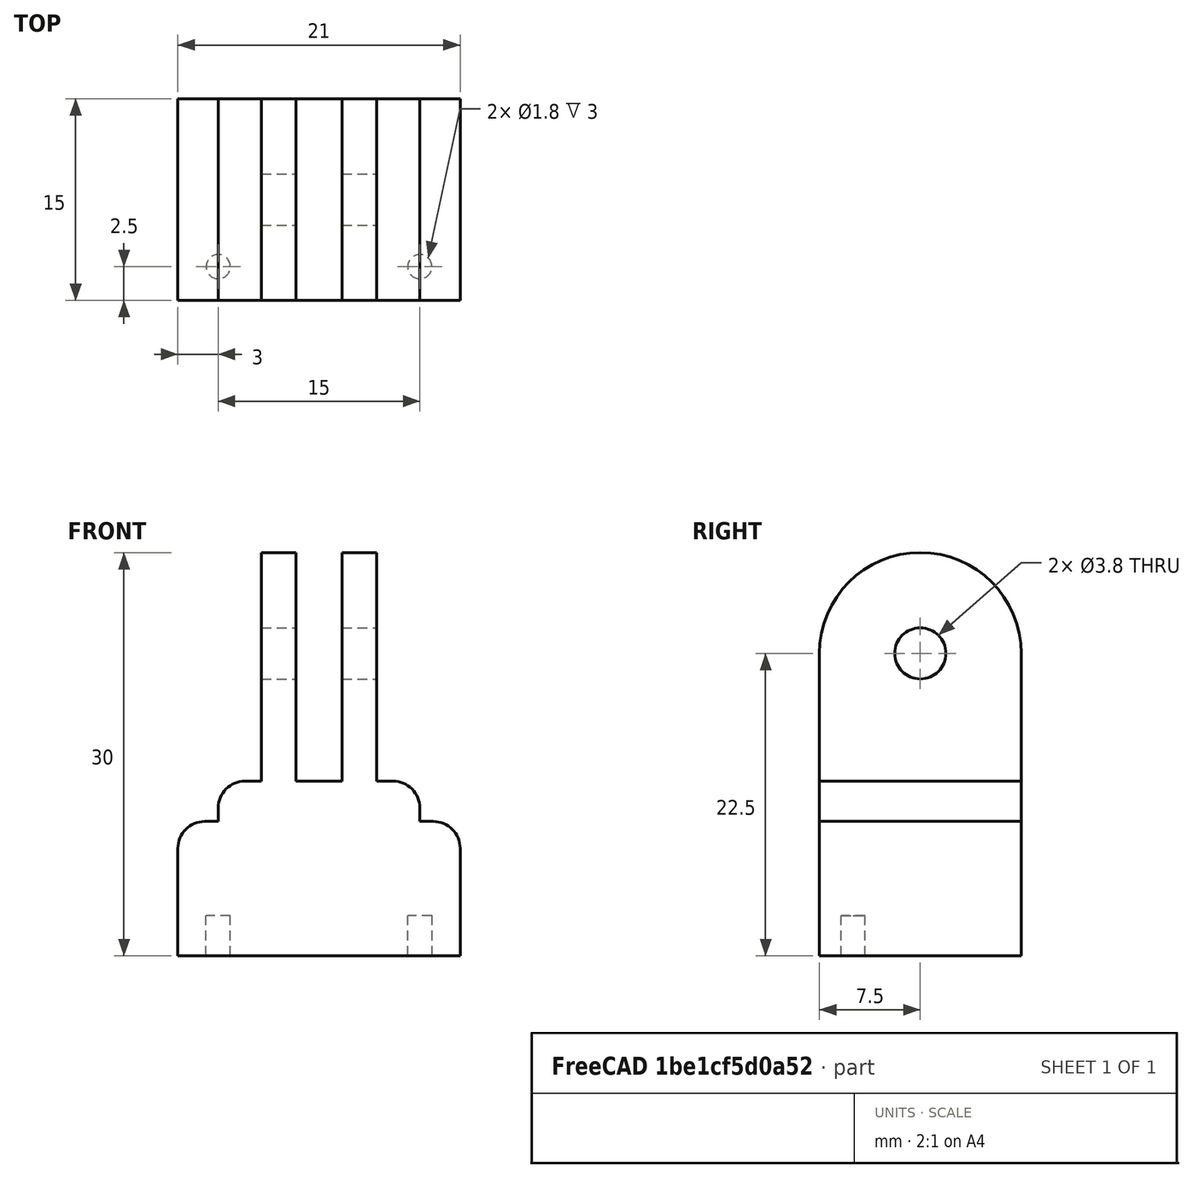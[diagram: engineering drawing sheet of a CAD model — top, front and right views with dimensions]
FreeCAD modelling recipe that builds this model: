
FCSTD DOCUMENT  (FreeCAD 0.19R23578 (Git))
Label: TCS3472RGBSensorSquare
License: FreeArt
LicenseURL: http://artlibre.org/licence/lal
objects: Part::Fillet×2, Spreadsheet::Sheet×1, Part::Cylinder×1, Part::FeaturePython×1, Part::Box×1, Part::Feature×1, Part::MultiFuse×1, Part::Cut×1, App::Part×1
note: 8 computed .brp shape members not serialized (recipe doc carries the construction recipe); baked Part::Feature solids carry a one-line shape summary decoded from their .brp

FEATURE [Spreadsheet::Sheet] Spreadsheet  label="p"
  cells = A1=pcb_x; B1(pcb_x)=21; A2=pcb_y; B2(pcb_y)=21; A3=pcb_z; B3(pcb_z)=1.7; A4=hole_dist_x; B4(hole_dist_x)=15; A5=hole_off_y; B5(hole_off_y)=2.5; A6=hole_r; B6(hole_r)=0.9; A7=sensor_hole_x; B7(sensor_hole_x)=2.6; A8=wall; B8(wall)=3; A9=stick_x; B9(stick_x)==pcb_x; A10=stick_y; B10(stick_y)=15; A11=stick_length; B11(stick_length)=10
FEATURE [Part::Cylinder] Cylinder  label="bolt hole"
  Angle = 360
  AttacherType = Attacher::AttachEngine3D
  Height = 3
  Radius = 0.9
  expr: Radius = <<p>>.hole_r
  expr: Height = <<p>>.wall
FEATURE [Part::FeaturePython] Array  label="bolt hole array"  # Draft array (typed FeaturePython)
  Angle = 360
  ArrayType = 0
  Axis = (0,0,1)
  Base = -> Cylinder
  Center = (0,0,0)
  Fuse = false
  IntervalAxis = (0,0,0)
  IntervalX = (15,0,0)
  IntervalY = (0,1,0)
  IntervalZ = (0,0,1)
  NumberPolar = 1
  NumberX = 2
  NumberY = 1
  NumberZ = 1
  Placement = pos=(3,2.5,0) rot=(0,0,1;0rad)
  expr: .Placement.Base.x = (<<p>>.pcb_x - <<p>>.hole_dist_x) / 2
  expr: .IntervalX.x = <<p>>.hole_dist_x
  expr: .Placement.Base.y = <<p>>.hole_off_y
FEATURE [Part::Box] Box002  label="stick cube"
  AttacherType = Attacher::AttachEngine3D
  Height = 10
  Length = 21
  Width = 15
  expr: Length = Spreadsheet.stick_x
  expr: Width = <<p>>.stick_y
  expr: Height = <<p>>.stick_length
FEATURE [Part::Feature] Cut001001  label="side 2 cut001"
  Placement = pos=(10.5,7.5,10) rot=(0,0,1;1.5708rad)
  shape: bbox 15 x 15 x 20 mm, 16 faces (baked)
  expr: .Placement.Base.y = <<p>>.stick_y / 2
  expr: .Placement.Base.x = Spreadsheet.stick_x / 2
  expr: .Placement.Base.z = <<p>>.stick_length
FEATURE [Part::Fillet] Fillet  label="stick cube fillet"
  Base = -> Box002
  Edges = 2 edges r=2: [Edge2,Edge6]
FEATURE [Part::MultiFuse] Fusion  label="holder fusion"
  Shapes = -> [Cut001001,Fillet]
FEATURE [Part::Fillet] Fillet001  label="holder fillet"
  Base = -> Fusion
  Edges = 2 edges r=2: [Edge47,Edge48]
FEATURE [Part::Cut] Cut  label="sensor cut"
  Base = -> Fillet001
  Tool = -> Array
FEATURE [App::Part] Part  label="TCS3472 sensor part"
  Group = -> [Cut]
  Origin = -> Origin
